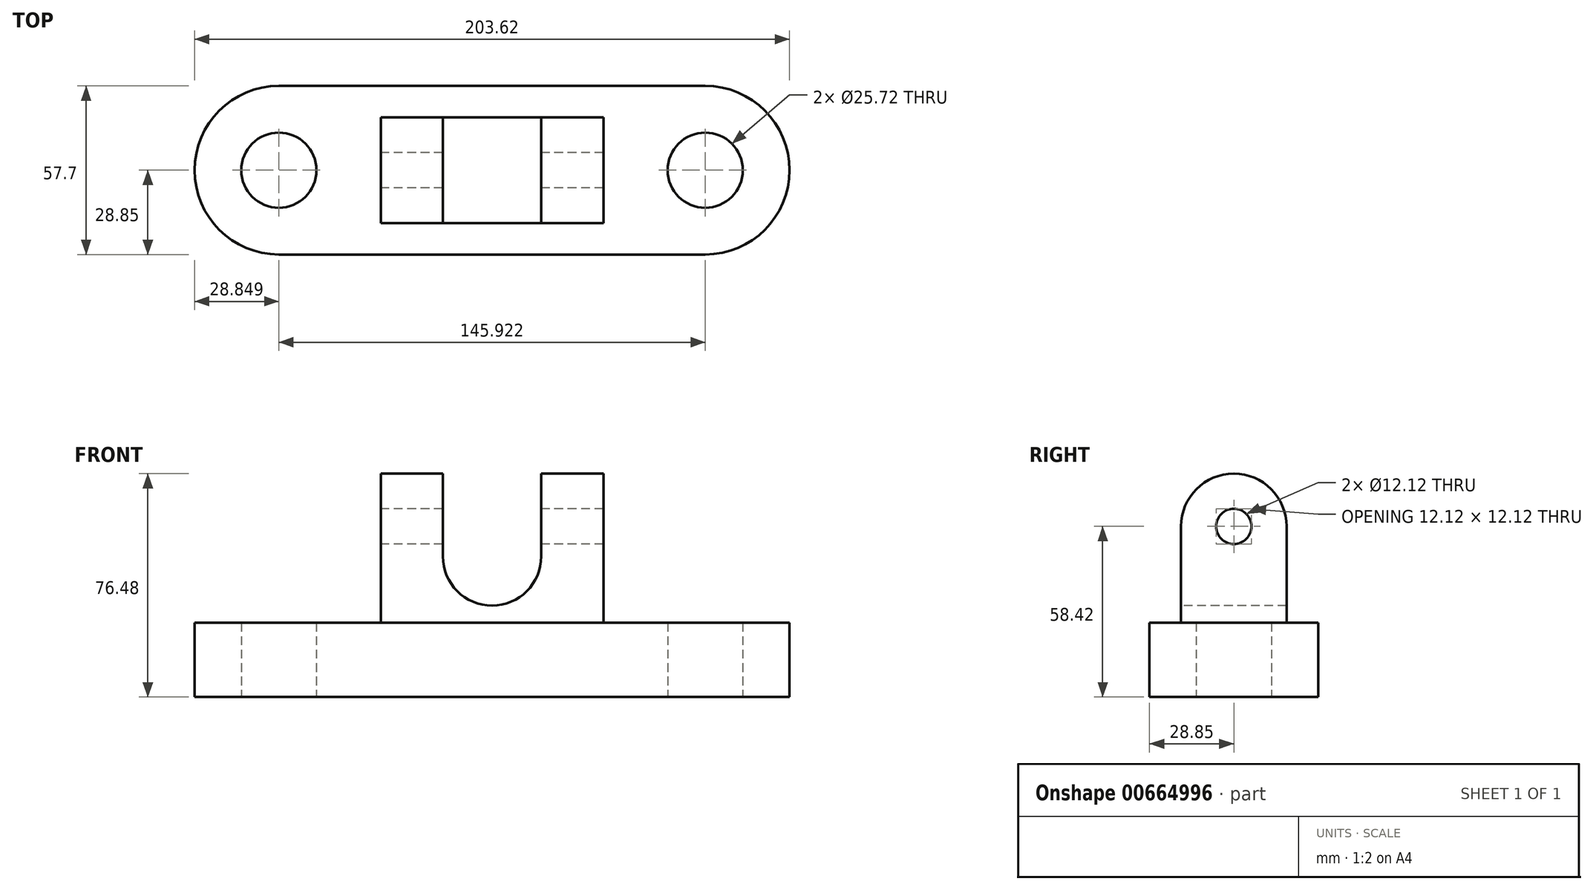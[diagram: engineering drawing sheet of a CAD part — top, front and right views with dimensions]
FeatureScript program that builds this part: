
annotation { "Feature Type Name" : "Feature", "Feature Type Description" : "" }
export const myFeature = defineFeature(function(context is Context, id is Id, definition is map)
    precondition{}
    {
        {
            var Q0;
            Q0=qCreatedBy(makeId("Top.planeOp"),FACE);
            var sketch = newSketch(context, id + "F0", { "sketchPlane" : qUnion([Q0])});
            skLineSegment(sketch, "E0.bottom", {"start": v(-72.96, 28.85) * mm, "end": v(72.96, 28.85) * mm});
            skLineSegment(sketch, "E0.top", {"start": v(-72.96, -28.85) * mm, "end": v(72.96, -28.85) * mm});
            skPoint(sketch, "E0.middle", {"position": v(0, 0) * mm});
            skArc(sketch, "E1", {"start": v(-72.96, 28.85) * mm, "mid": v(-101.81, 0) * mm, "end": v(-72.96, -28.85) * mm});
            skArc(sketch, "E2", {"start": v(72.96, -28.85) * mm, "mid": v(101.81, 0) * mm, "end": v(72.96, 28.85) * mm});
            skCircle(sketch, "E3", {"center": v(-72.96, 0) * mm, "radius": 12.86 * mm});
            skCircle(sketch, "E4", {"center": v(72.96, 0) * mm, "radius": 12.86 * mm});
            skLineSegment(sketch, "E5.bottom", {"start": v(-38.1, -18.06) * mm, "end": v(38.1, -18.06) * mm});
            skLineSegment(sketch, "E5.top", {"start": v(-38.1, 18.06) * mm, "end": v(38.1, 18.06) * mm});
            skLineSegment(sketch, "E5.left", {"start": v(-38.1, -18.06) * mm, "end": v(-38.1, 18.06) * mm});
            skLineSegment(sketch, "E5.right", {"start": v(38.1, -18.06) * mm, "end": v(38.1, 18.06) * mm});
            skSolve(sketch);
        }
        {
            var Q0;
            Q0=makeQuery(id+"F0.imprint","IMPRINT",FACE,{"disambiguationData":[TD([[makeQuery(id+"F0.imprint","IMPRINT",EDGE,{"derivedFrom":sQuery(id+"F0.wireOp",EDGE,"E5.bottom")}),1.0]])]});
            extrude(context, id + "F1", {"entities" : qUnion([Q0]), "depth" : 58.42 * mm, "offsetDistance" : 25.4 * mm});
        }
        {
            var Q0;
            Q0 = qSketchRegion(id + "F0", true);
            extrude(context, id + "F2", {"entities" : qUnion([Q0]), "operationType" : NewBodyOperationType.ADD, "depth" : 25.4 * mm, "offsetDistance" : 25.4 * mm});
        }
        {
            var Q0;
            Q0=makeQuery(id+"F1.opExtrude","SWEPT_FACE",FACE,{"disambiguationData":[OSD([sQuery(id+"F0.wireOp",EDGE,"E5.left")])]});
            var sketch = newSketch(context, id + "F3", { "sketchPlane" : qUnion([Q0])});
            skArc(sketch, "E6", {"start": v(18.06, 58.42) * mm, "mid": v(0, 76.48) * mm, "end": v(-18.06, 58.42) * mm});
            skCircle(sketch, "E7", {"center": v(0, 58.42) * mm, "radius": 6.06 * mm});
            skSolve(sketch);
        }
        {
            var Q0;
            Q0 = qSketchRegion(id + "F3", true);
            var Q1;
            Q1=makeQuery(id+"F3.imprint","IMPRINT",FACE,{"disambiguationData":[TD([[makeQuery(id+"F3.imprint","IMPRINT",EDGE,{"derivedFrom":sQuery(id+"F3.wireOp",EDGE,"E6")}),1.0]])]});
            extrude(context, id + "F4", {"entities" : qUnion([Q0, Q1]), "operationType" : NewBodyOperationType.ADD, "oppositeDirection" : true, "depth" : 76.2 * mm, "offsetDistance" : 25.4 * mm});
        }
        {
            var Q0;
            Q0 = qSketchRegion(id + "F3", true);
            extrude(context, id + "F5", {"entities" : qUnion([Q0]), "operationType" : NewBodyOperationType.REMOVE, "oppositeDirection" : true, "depth" : 76.2 * mm, "offsetDistance" : 25.4 * mm});
        }
        {
            var Q0;
            Q0=qCreatedBy(makeId("Front.planeOp"),FACE);
            var sketch = newSketch(context, id + "F6", { "sketchPlane" : qUnion([Q0])});
            skLineSegment(sketch, "E8.top", {"start": v(-16.83, 103.53) * mm, "end": v(16.83, 103.53) * mm});
            skLineSegment(sketch, "E8.left", {"start": v(-16.83, 48.14) * mm, "end": v(-16.83, 103.53) * mm});
            skLineSegment(sketch, "E8.right", {"start": v(16.83, 48.14) * mm, "end": v(16.83, 103.53) * mm});
            skPoint(sketch, "E8.middle", {"position": v(0, 75.84) * mm});
            skArc(sketch, "E9", {"start": v(-16.83, 48.14) * mm, "mid": v(0, 31.31) * mm, "end": v(16.83, 48.14) * mm});
            skSolve(sketch);
        }
        {
            var Q0;
            Q0=makeQuery(id+"F6.imprint","IMPRINT",FACE,{"disambiguationData":[TD([[makeQuery(id+"F6.imprint","IMPRINT",EDGE,{"derivedFrom":sQuery(id+"F6.wireOp",EDGE,"E8.top")}),-1.0]])]});
            extrude(context, id + "F7", {"entities" : qUnion([Q0]), "operationType" : NewBodyOperationType.REMOVE, "endBound" : BoundingType.SYMMETRIC, "oppositeDirection" : true, "depth" : 76.2 * mm, "offsetDistance" : 25.4 * mm});
        }
    });
